# Revit family: Fexa_linea_litoral_pano_fijo
name_source: partatom
category: Ventanas
units: mm (PartAtom-declared; Revit-internal decimal feet)

## family parameters
Anfitrión = Muro
Compartido = No
Corte con vacíos al cargar = No
Número OmniClass = 23.30.20.00
Punto de cálculo de habitación = No
Siempre vertical = Sí
Título OmniClass = Windows

## types (1)
- 1 x 2
    Abatible = Sí
    Acristalamiento = 4 a 26 mm
    Altura de antepecho por defecto = 0.8 m
    Cierre de muro = Por anfitrión
    Construcción analítica = <Ninguno>
    Definir propiedades térmicas por = Tipo esquemático
    Dimensiones Maximas = 2200 mm (a) x 2500mm (h)
    Direccion = Favario (ex. Biedma)8000 2000 Rosario Santa Fe
    Espesor de perfileria = 1.25
    Fabricante = Fexa
    Funcion = Interior
    Material Junta = Sellador primario butillo
    Modelo = Linea Litoral
    Motorizada = No
    Numero Whatsapp = +54 9 341 5705025
    Oscilobatiente = No
    Pais = Argentina
    Practicable = No
    Secciones = Marco 75 mm
    URL = www.fexainfo.com.ar
    mat bisagras = Fexa_Bisagra color negro
    mat burlete = Sellador primario butillo
    mat cristal = Cristal para dvh
    mat cubrejuntas = Fexa_ aluminio pintado _blanco Brillante
    mat marco = Fexa_ aluminio pintado _blanco Brillante
    mat premarco = Fexa_ aluminio anodizado _peltre
    mat tornillos = Tornillo de acero
    material carcasa = Fexa_ aluminio pintado _blanco Brillante
    numero telefono = 0341 409 5070
    pagina web = www.fexa.com.ar
